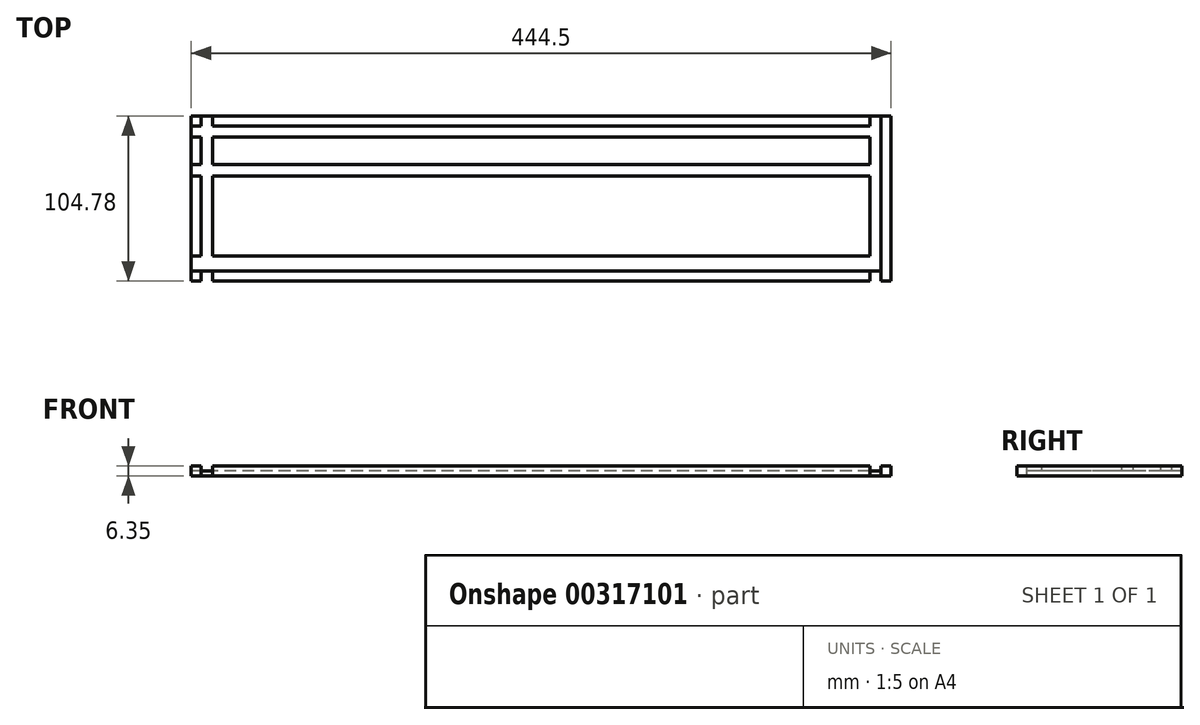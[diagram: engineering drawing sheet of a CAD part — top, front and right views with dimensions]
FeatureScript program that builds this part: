
annotation { "Feature Type Name" : "Feature", "Feature Type Description" : "" }
export const myFeature = defineFeature(function(context is Context, id is Id, definition is map)
    precondition{}
    {
        {
            var Q0;
            Q0=qCreatedBy(makeId("Top.planeOp"),FACE);
            var sketch = newSketch(context, id + "F0", { "sketchPlane" : qUnion([Q0])});
            skLineSegment(sketch, "E0.bottom", {"start": v(222.25, 52.39) * mm, "end": v(-222.25, 52.39) * mm});
            skLineSegment(sketch, "E0.top", {"start": v(222.25, -52.39) * mm, "end": v(-222.25, -52.39) * mm});
            skLineSegment(sketch, "E0.left", {"start": v(222.25, 52.39) * mm, "end": v(222.25, -52.39) * mm});
            skLineSegment(sketch, "E0.right", {"start": v(-222.25, 52.39) * mm, "end": v(-222.25, -52.39) * mm});
            skPoint(sketch, "E0.middle", {"position": v(0, 0) * mm});
            skLineSegment(sketch, "E1.0", {"start": v(-215.9, 52.39) * mm, "end": v(-215.9, -52.39) * mm});
            skLineSegment(sketch, "E2.0", {"start": v(-208.76, 52.39) * mm, "end": v(-208.76, -52.39) * mm});
            skLineSegment(sketch, "E3.0", {"start": v(215.9, 52.39) * mm, "end": v(215.9, -52.39) * mm});
            skLineSegment(sketch, "E4.0", {"start": v(208.76, 52.39) * mm, "end": v(208.76, -52.39) * mm});
            skLineSegment(sketch, "E5", {"start": v(215.9, -46.04) * mm, "end": v(-222.25, -46.04) * mm});
            skLineSegment(sketch, "E6.0", {"start": v(215.9, -36.51) * mm, "end": v(-222.25, -36.51) * mm});
            skLineSegment(sketch, "E7.0", {"start": v(215.9, 14.29) * mm, "end": v(-222.25, 14.29) * mm});
            skLineSegment(sketch, "E8.0", {"start": v(215.9, 21.43) * mm, "end": v(-222.25, 21.43) * mm});
            skLineSegment(sketch, "E9", {"start": v(215.9, 46.04) * mm, "end": v(-222.25, 46.04) * mm});
            skLineSegment(sketch, "E10.0", {"start": v(215.9, 38.9) * mm, "end": v(-222.25, 38.9) * mm});
            skSolve(sketch);
        }
        {
            var Q0;
            {var subQ0=sQuery(id+"F0.wireOp",EDGE,"E2.0");var subQ1=sQuery(id+"F0.wireOp",EDGE,"E0.bottom");var subQ2=makeQuery(id+"F0.imprint","INTERSECT",VERTEX,{"derivedFrom":[subQ1,subQ0]});Q0=makeQuery(id+"F0.imprint","IMPRINT",FACE,{"disambiguationData":[TD([[makeQuery(id+"F0.imprint","IMPRINT",EDGE,{"disambiguationData":[TD([[subQ2,1.0]])],"derivedFrom":subQ1}),1.0]])]});}
            var Q1;
            {var subQ0=sQuery(id+"F0.wireOp",EDGE,"E2.0");var subQ1=sQuery(id+"F0.wireOp",EDGE,"E0.top");var subQ2=makeQuery(id+"F0.imprint","INTERSECT",VERTEX,{"derivedFrom":[subQ1,subQ0]});Q1=makeQuery(id+"F0.imprint","IMPRINT",FACE,{"disambiguationData":[TD([[makeQuery(id+"F0.imprint","IMPRINT",EDGE,{"disambiguationData":[TD([[subQ2,1.0]])],"derivedFrom":subQ1}),-1.0]])]});}
            var Q2;
            {var subQ0=sQuery(id+"F0.wireOp",EDGE,"E7.0");var subQ1=sQuery(id+"F0.wireOp",EDGE,"E1.0");var subQ2=makeQuery(id+"F0.imprint","INTERSECT",VERTEX,{"derivedFrom":[subQ1,subQ0]});Q2=makeQuery(id+"F0.imprint","IMPRINT",FACE,{"disambiguationData":[TD([[makeQuery(id+"F0.imprint","IMPRINT",EDGE,{"disambiguationData":[TD([[subQ2,-1.0]])],"derivedFrom":subQ1}),1.0]])]});}
            var Q3;
            {var subQ0=sQuery(id+"F0.wireOp",EDGE,"E10.0");var subQ1=sQuery(id+"F0.wireOp",EDGE,"E1.0");var subQ2=makeQuery(id+"F0.imprint","INTERSECT",VERTEX,{"derivedFrom":[subQ1,subQ0]});Q3=makeQuery(id+"F0.imprint","IMPRINT",FACE,{"disambiguationData":[TD([[makeQuery(id+"F0.imprint","IMPRINT",EDGE,{"disambiguationData":[TD([[subQ2,-1.0]])],"derivedFrom":subQ1}),1.0]])]});}
            var Q4;
            {var subQ0=sQuery(id+"F0.wireOp",EDGE,"E9");var subQ1=sQuery(id+"F0.wireOp",EDGE,"E2.0");var subQ2=makeQuery(id+"F0.imprint","INTERSECT",VERTEX,{"derivedFrom":[subQ1,subQ0]});Q4=makeQuery(id+"F0.imprint","IMPRINT",FACE,{"disambiguationData":[TD([[makeQuery(id+"F0.imprint","IMPRINT",EDGE,{"disambiguationData":[TD([[subQ2,-1.0]])],"derivedFrom":subQ1}),1.0]])]});}
            var Q5;
            {var subQ0=sQuery(id+"F0.wireOp",EDGE,"E8.0");var subQ1=sQuery(id+"F0.wireOp",EDGE,"E2.0");var subQ2=makeQuery(id+"F0.imprint","INTERSECT",VERTEX,{"derivedFrom":[subQ1,subQ0]});Q5=makeQuery(id+"F0.imprint","IMPRINT",FACE,{"disambiguationData":[TD([[makeQuery(id+"F0.imprint","IMPRINT",EDGE,{"disambiguationData":[TD([[subQ2,-1.0]])],"derivedFrom":subQ1}),1.0]])]});}
            var Q6;
            {var subQ4=sQuery(id+"F0.wireOp",EDGE,"E0.left");Q6=makeQuery(id+"F0.imprint","IMPRINT",FACE,{"disambiguationData":[TD([[makeQuery(id+"F0.imprint","IMPRINT",EDGE,{"derivedFrom":subQ4}),-1.0]])]});}
            var Q7;
            {var subQ0=sQuery(id+"F0.wireOp",EDGE,"E6.0");var subQ1=sQuery(id+"F0.wireOp",EDGE,"E0.right");var subQ2=makeQuery(id+"F0.imprint","INTERSECT",VERTEX,{"derivedFrom":[subQ1,subQ0]});Q7=makeQuery(id+"F0.imprint","IMPRINT",FACE,{"disambiguationData":[TD([[makeQuery(id+"F0.imprint","IMPRINT",EDGE,{"disambiguationData":[TD([[subQ2,1.0]])],"derivedFrom":subQ1}),1.0]])]});}
            var Q8;
            {var subQ0=sQuery(id+"F0.wireOp",EDGE,"E6.0");var subQ1=sQuery(id+"F0.wireOp",EDGE,"E2.0");var subQ2=makeQuery(id+"F0.imprint","INTERSECT",VERTEX,{"derivedFrom":[subQ1,subQ0]});Q8=makeQuery(id+"F0.imprint","IMPRINT",FACE,{"disambiguationData":[TD([[makeQuery(id+"F0.imprint","IMPRINT",EDGE,{"disambiguationData":[TD([[subQ2,-1.0]])],"derivedFrom":subQ1}),1.0]])]});}
            var Q9;
            {var subQ0=sQuery(id+"F0.wireOp",EDGE,"E7.0");var subQ1=sQuery(id+"F0.wireOp",EDGE,"E2.0");var subQ2=makeQuery(id+"F0.imprint","INTERSECT",VERTEX,{"derivedFrom":[subQ1,subQ0]});Q9=makeQuery(id+"F0.imprint","IMPRINT",FACE,{"disambiguationData":[TD([[makeQuery(id+"F0.imprint","IMPRINT",EDGE,{"disambiguationData":[TD([[subQ2,-1.0]])],"derivedFrom":subQ1}),1.0]])]});}
            var Q10;
            {var subQ0=sQuery(id+"F0.wireOp",EDGE,"E10.0");var subQ1=sQuery(id+"F0.wireOp",EDGE,"E2.0");var subQ2=makeQuery(id+"F0.imprint","INTERSECT",VERTEX,{"derivedFrom":[subQ1,subQ0]});Q10=makeQuery(id+"F0.imprint","IMPRINT",FACE,{"disambiguationData":[TD([[makeQuery(id+"F0.imprint","IMPRINT",EDGE,{"disambiguationData":[TD([[subQ2,-1.0]])],"derivedFrom":subQ1}),1.0]])]});}
            var Q11;
            {var subQ0=sQuery(id+"F0.wireOp",EDGE,"E9");var subQ1=sQuery(id+"F0.wireOp",EDGE,"E0.right");var subQ2=makeQuery(id+"F0.imprint","INTERSECT",VERTEX,{"derivedFrom":[subQ1,subQ0]});Q11=makeQuery(id+"F0.imprint","IMPRINT",FACE,{"disambiguationData":[TD([[makeQuery(id+"F0.imprint","IMPRINT",EDGE,{"disambiguationData":[TD([[subQ2,-1.0]])],"derivedFrom":subQ1}),1.0]])]});}
            var Q12;
            {var subQ0=sQuery(id+"F0.wireOp",EDGE,"E1.0");var subQ1=sQuery(id+"F0.wireOp",EDGE,"E0.bottom");var subQ2=makeQuery(id+"F0.imprint","INTERSECT",VERTEX,{"derivedFrom":[subQ1,subQ0]});Q12=makeQuery(id+"F0.imprint","IMPRINT",FACE,{"disambiguationData":[TD([[makeQuery(id+"F0.imprint","IMPRINT",EDGE,{"disambiguationData":[TD([[subQ2,1.0]])],"derivedFrom":subQ1}),1.0]])]});}
            var Q13;
            {var subQ0=sQuery(id+"F0.wireOp",EDGE,"E3.0");var subQ1=sQuery(id+"F0.wireOp",EDGE,"E0.bottom");var subQ2=makeQuery(id+"F0.imprint","INTERSECT",VERTEX,{"derivedFrom":[subQ1,subQ0]});Q13=makeQuery(id+"F0.imprint","IMPRINT",FACE,{"disambiguationData":[TD([[makeQuery(id+"F0.imprint","IMPRINT",EDGE,{"disambiguationData":[TD([[subQ2,-1.0]])],"derivedFrom":subQ1}),1.0]])]});}
            var Q14;
            {var subQ0=sQuery(id+"F0.wireOp",EDGE,"E0.right");var subQ1=sQuery(id+"F0.wireOp",EDGE,"E0.bottom");var subQ2=makeQuery(id+"F0.imprint","INTERSECT",VERTEX,{"derivedFrom":[subQ1,subQ0]});Q14=makeQuery(id+"F0.imprint","IMPRINT",FACE,{"disambiguationData":[TD([[makeQuery(id+"F0.imprint","IMPRINT",EDGE,{"disambiguationData":[TD([[subQ2,1.0]])],"derivedFrom":subQ1}),1.0]])]});}
            var Q15;
            {var subQ0=sQuery(id+"F0.wireOp",EDGE,"E8.0");var subQ1=sQuery(id+"F0.wireOp",EDGE,"E1.0");var subQ2=makeQuery(id+"F0.imprint","INTERSECT",VERTEX,{"derivedFrom":[subQ1,subQ0]});Q15=makeQuery(id+"F0.imprint","IMPRINT",FACE,{"disambiguationData":[TD([[makeQuery(id+"F0.imprint","IMPRINT",EDGE,{"disambiguationData":[TD([[subQ2,-1.0]])],"derivedFrom":subQ1}),1.0]])]});}
            var Q16;
            {var subQ0=sQuery(id+"F0.wireOp",EDGE,"E9");var subQ1=sQuery(id+"F0.wireOp",EDGE,"E1.0");var subQ2=makeQuery(id+"F0.imprint","INTERSECT",VERTEX,{"derivedFrom":[subQ1,subQ0]});Q16=makeQuery(id+"F0.imprint","IMPRINT",FACE,{"disambiguationData":[TD([[makeQuery(id+"F0.imprint","IMPRINT",EDGE,{"disambiguationData":[TD([[subQ2,-1.0]])],"derivedFrom":subQ1}),1.0]])]});}
            var Q17;
            {var subQ0=sQuery(id+"F0.wireOp",EDGE,"E8.0");var subQ1=sQuery(id+"F0.wireOp",EDGE,"E3.0");var subQ2=makeQuery(id+"F0.imprint","INTERSECT",VERTEX,{"derivedFrom":[subQ1,subQ0]});Q17=makeQuery(id+"F0.imprint","IMPRINT",FACE,{"disambiguationData":[TD([[makeQuery(id+"F0.imprint","IMPRINT",EDGE,{"disambiguationData":[TD([[subQ2,1.0]])],"derivedFrom":subQ1}),-1.0]])]});}
            var Q18;
            {var subQ0=sQuery(id+"F0.wireOp",EDGE,"E8.0");var subQ1=sQuery(id+"F0.wireOp",EDGE,"E0.right");var subQ2=makeQuery(id+"F0.imprint","INTERSECT",VERTEX,{"derivedFrom":[subQ1,subQ0]});Q18=makeQuery(id+"F0.imprint","IMPRINT",FACE,{"disambiguationData":[TD([[makeQuery(id+"F0.imprint","IMPRINT",EDGE,{"disambiguationData":[TD([[subQ2,1.0]])],"derivedFrom":subQ1}),1.0]])]});}
            var Q19;
            {var subQ0=sQuery(id+"F0.wireOp",EDGE,"E7.0");var subQ1=sQuery(id+"F0.wireOp",EDGE,"E0.right");var subQ2=makeQuery(id+"F0.imprint","INTERSECT",VERTEX,{"derivedFrom":[subQ1,subQ0]});Q19=makeQuery(id+"F0.imprint","IMPRINT",FACE,{"disambiguationData":[TD([[makeQuery(id+"F0.imprint","IMPRINT",EDGE,{"disambiguationData":[TD([[subQ2,1.0]])],"derivedFrom":subQ1}),1.0]])]});}
            var Q20;
            {var subQ0=sQuery(id+"F0.wireOp",EDGE,"E5");var subQ1=sQuery(id+"F0.wireOp",EDGE,"E0.right");var subQ2=makeQuery(id+"F0.imprint","INTERSECT",VERTEX,{"derivedFrom":[subQ1,subQ0]});Q20=makeQuery(id+"F0.imprint","IMPRINT",FACE,{"disambiguationData":[TD([[makeQuery(id+"F0.imprint","IMPRINT",EDGE,{"disambiguationData":[TD([[subQ2,1.0]])],"derivedFrom":subQ1}),1.0]])]});}
            var Q21;
            {var subQ0=sQuery(id+"F0.wireOp",EDGE,"E5");var subQ1=sQuery(id+"F0.wireOp",EDGE,"E3.0");var subQ2=makeQuery(id+"F0.imprint","INTERSECT",VERTEX,{"derivedFrom":[subQ1,subQ0]});Q21=makeQuery(id+"F0.imprint","IMPRINT",FACE,{"disambiguationData":[TD([[makeQuery(id+"F0.imprint","IMPRINT",EDGE,{"disambiguationData":[TD([[subQ2,1.0]])],"derivedFrom":subQ1}),-1.0]])]});}
            var Q22;
            {var subQ0=sQuery(id+"F0.wireOp",EDGE,"E9");var subQ1=sQuery(id+"F0.wireOp",EDGE,"E3.0");var subQ2=makeQuery(id+"F0.imprint","INTERSECT",VERTEX,{"derivedFrom":[subQ1,subQ0]});Q22=makeQuery(id+"F0.imprint","IMPRINT",FACE,{"disambiguationData":[TD([[makeQuery(id+"F0.imprint","IMPRINT",EDGE,{"disambiguationData":[TD([[subQ2,-1.0]])],"derivedFrom":subQ1}),-1.0]])]});}
            var Q23;
            {var subQ0=sQuery(id+"F0.wireOp",EDGE,"E7.0");var subQ1=sQuery(id+"F0.wireOp",EDGE,"E3.0");var subQ2=makeQuery(id+"F0.imprint","INTERSECT",VERTEX,{"derivedFrom":[subQ1,subQ0]});Q23=makeQuery(id+"F0.imprint","IMPRINT",FACE,{"disambiguationData":[TD([[makeQuery(id+"F0.imprint","IMPRINT",EDGE,{"disambiguationData":[TD([[subQ2,1.0]])],"derivedFrom":subQ1}),-1.0]])]});}
            var Q24;
            {var subQ0=sQuery(id+"F0.wireOp",EDGE,"E6.0");var subQ1=sQuery(id+"F0.wireOp",EDGE,"E1.0");var subQ2=makeQuery(id+"F0.imprint","INTERSECT",VERTEX,{"derivedFrom":[subQ1,subQ0]});Q24=makeQuery(id+"F0.imprint","IMPRINT",FACE,{"disambiguationData":[TD([[makeQuery(id+"F0.imprint","IMPRINT",EDGE,{"disambiguationData":[TD([[subQ2,-1.0]])],"derivedFrom":subQ1}),1.0]])]});}
            var Q25;
            {var subQ0=sQuery(id+"F0.wireOp",EDGE,"E0.right");var subQ1=sQuery(id+"F0.wireOp",EDGE,"E0.top");var subQ2=makeQuery(id+"F0.imprint","INTERSECT",VERTEX,{"derivedFrom":[subQ1,subQ0]});Q25=makeQuery(id+"F0.imprint","IMPRINT",FACE,{"disambiguationData":[TD([[makeQuery(id+"F0.imprint","IMPRINT",EDGE,{"disambiguationData":[TD([[subQ2,1.0]])],"derivedFrom":subQ1}),-1.0]])]});}
            var Q26;
            {var subQ0=sQuery(id+"F0.wireOp",EDGE,"E6.0");var subQ1=sQuery(id+"F0.wireOp",EDGE,"E3.0");var subQ2=makeQuery(id+"F0.imprint","INTERSECT",VERTEX,{"derivedFrom":[subQ1,subQ0]});Q26=makeQuery(id+"F0.imprint","IMPRINT",FACE,{"disambiguationData":[TD([[makeQuery(id+"F0.imprint","IMPRINT",EDGE,{"disambiguationData":[TD([[subQ2,1.0]])],"derivedFrom":subQ1}),-1.0]])]});}
            var Q27;
            Q27=sQuery(id+"F0.wireOp",EDGE,"E0.right");
            var Q28;
            Q28=sQuery(id+"F0.wireOp",EDGE,"E0.bottom");
            var Q29;
            Q29=sQuery(id+"F0.wireOp",EDGE,"E0.top");
            var Q30;
            Q30=sQuery(id+"F0.wireOp",EDGE,"E0.left");
            extrude(context, id + "F1", {"entities" : qUnion([Q0, Q1, Q2, Q3, Q4, Q5, Q6, Q7, Q8, Q9, Q10, Q11, Q12, Q13, Q14, Q15, Q16, Q17, Q18, Q19, Q20, Q21, Q22, Q23, Q24, Q25, Q26]), "surfaceEntities" : qUnion([Q27, Q28, Q29, Q30]), "oppositeDirection" : true, "depth" : 6.35 * mm});
        }
        {
            var Q0;
            {var subQ0=sQuery(id+"F0.wireOp",EDGE,"E6.0");var subQ1=sQuery(id+"F0.wireOp",EDGE,"E1.0");var subQ2=makeQuery(id+"F0.imprint","INTERSECT",VERTEX,{"derivedFrom":[subQ1,subQ0]});Q0=makeQuery(id+"F0.imprint","IMPRINT",FACE,{"disambiguationData":[TD([[makeQuery(id+"F0.imprint","IMPRINT",EDGE,{"disambiguationData":[TD([[subQ2,-1.0]])],"derivedFrom":subQ1}),1.0]])]});}
            var Q1;
            {var subQ0=sQuery(id+"F0.wireOp",EDGE,"E7.0");var subQ1=sQuery(id+"F0.wireOp",EDGE,"E1.0");var subQ2=makeQuery(id+"F0.imprint","INTERSECT",VERTEX,{"derivedFrom":[subQ1,subQ0]});Q1=makeQuery(id+"F0.imprint","IMPRINT",FACE,{"disambiguationData":[TD([[makeQuery(id+"F0.imprint","IMPRINT",EDGE,{"disambiguationData":[TD([[subQ2,-1.0]])],"derivedFrom":subQ1}),1.0]])]});}
            var Q2;
            {var subQ0=sQuery(id+"F0.wireOp",EDGE,"E8.0");var subQ1=sQuery(id+"F0.wireOp",EDGE,"E1.0");var subQ2=makeQuery(id+"F0.imprint","INTERSECT",VERTEX,{"derivedFrom":[subQ1,subQ0]});Q2=makeQuery(id+"F0.imprint","IMPRINT",FACE,{"disambiguationData":[TD([[makeQuery(id+"F0.imprint","IMPRINT",EDGE,{"disambiguationData":[TD([[subQ2,-1.0]])],"derivedFrom":subQ1}),1.0]])]});}
            var Q3;
            {var subQ0=sQuery(id+"F0.wireOp",EDGE,"E10.0");var subQ1=sQuery(id+"F0.wireOp",EDGE,"E1.0");var subQ2=makeQuery(id+"F0.imprint","INTERSECT",VERTEX,{"derivedFrom":[subQ1,subQ0]});Q3=makeQuery(id+"F0.imprint","IMPRINT",FACE,{"disambiguationData":[TD([[makeQuery(id+"F0.imprint","IMPRINT",EDGE,{"disambiguationData":[TD([[subQ2,-1.0]])],"derivedFrom":subQ1}),1.0]])]});}
            var Q4;
            {var subQ0=sQuery(id+"F0.wireOp",EDGE,"E9");var subQ1=sQuery(id+"F0.wireOp",EDGE,"E1.0");var subQ2=makeQuery(id+"F0.imprint","INTERSECT",VERTEX,{"derivedFrom":[subQ1,subQ0]});Q4=makeQuery(id+"F0.imprint","IMPRINT",FACE,{"disambiguationData":[TD([[makeQuery(id+"F0.imprint","IMPRINT",EDGE,{"disambiguationData":[TD([[subQ2,-1.0]])],"derivedFrom":subQ1}),1.0]])]});}
            var Q5;
            {var subQ0=sQuery(id+"F0.wireOp",EDGE,"E1.0");var subQ1=sQuery(id+"F0.wireOp",EDGE,"E0.bottom");var subQ2=makeQuery(id+"F0.imprint","INTERSECT",VERTEX,{"derivedFrom":[subQ1,subQ0]});Q5=makeQuery(id+"F0.imprint","IMPRINT",FACE,{"disambiguationData":[TD([[makeQuery(id+"F0.imprint","IMPRINT",EDGE,{"disambiguationData":[TD([[subQ2,1.0]])],"derivedFrom":subQ1}),1.0]])]});}
            var Q6;
            {var subQ0=sQuery(id+"F0.wireOp",EDGE,"E9");var subQ1=sQuery(id+"F0.wireOp",EDGE,"E0.right");var subQ2=makeQuery(id+"F0.imprint","INTERSECT",VERTEX,{"derivedFrom":[subQ1,subQ0]});Q6=makeQuery(id+"F0.imprint","IMPRINT",FACE,{"disambiguationData":[TD([[makeQuery(id+"F0.imprint","IMPRINT",EDGE,{"disambiguationData":[TD([[subQ2,-1.0]])],"derivedFrom":subQ1}),1.0]])]});}
            var Q7;
            {var subQ0=sQuery(id+"F0.wireOp",EDGE,"E7.0");var subQ1=sQuery(id+"F0.wireOp",EDGE,"E0.right");var subQ2=makeQuery(id+"F0.imprint","INTERSECT",VERTEX,{"derivedFrom":[subQ1,subQ0]});Q7=makeQuery(id+"F0.imprint","IMPRINT",FACE,{"disambiguationData":[TD([[makeQuery(id+"F0.imprint","IMPRINT",EDGE,{"disambiguationData":[TD([[subQ2,1.0]])],"derivedFrom":subQ1}),1.0]])]});}
            var Q8;
            {var subQ0=sQuery(id+"F0.wireOp",EDGE,"E8.0");var subQ1=sQuery(id+"F0.wireOp",EDGE,"E2.0");var subQ2=makeQuery(id+"F0.imprint","INTERSECT",VERTEX,{"derivedFrom":[subQ1,subQ0]});Q8=makeQuery(id+"F0.imprint","IMPRINT",FACE,{"disambiguationData":[TD([[makeQuery(id+"F0.imprint","IMPRINT",EDGE,{"disambiguationData":[TD([[subQ2,-1.0]])],"derivedFrom":subQ1}),1.0]])]});}
            var Q9;
            {var subQ0=sQuery(id+"F0.wireOp",EDGE,"E9");var subQ1=sQuery(id+"F0.wireOp",EDGE,"E2.0");var subQ2=makeQuery(id+"F0.imprint","INTERSECT",VERTEX,{"derivedFrom":[subQ1,subQ0]});Q9=makeQuery(id+"F0.imprint","IMPRINT",FACE,{"disambiguationData":[TD([[makeQuery(id+"F0.imprint","IMPRINT",EDGE,{"disambiguationData":[TD([[subQ2,-1.0]])],"derivedFrom":subQ1}),1.0]])]});}
            var Q10;
            {var subQ0=sQuery(id+"F0.wireOp",EDGE,"E5");var subQ1=sQuery(id+"F0.wireOp",EDGE,"E0.right");var subQ2=makeQuery(id+"F0.imprint","INTERSECT",VERTEX,{"derivedFrom":[subQ1,subQ0]});Q10=makeQuery(id+"F0.imprint","IMPRINT",FACE,{"disambiguationData":[TD([[makeQuery(id+"F0.imprint","IMPRINT",EDGE,{"disambiguationData":[TD([[subQ2,1.0]])],"derivedFrom":subQ1}),1.0]])]});}
            var Q11;
            {var subQ0=sQuery(id+"F0.wireOp",EDGE,"E6.0");var subQ1=sQuery(id+"F0.wireOp",EDGE,"E2.0");var subQ2=makeQuery(id+"F0.imprint","INTERSECT",VERTEX,{"derivedFrom":[subQ1,subQ0]});Q11=makeQuery(id+"F0.imprint","IMPRINT",FACE,{"disambiguationData":[TD([[makeQuery(id+"F0.imprint","IMPRINT",EDGE,{"disambiguationData":[TD([[subQ2,-1.0]])],"derivedFrom":subQ1}),1.0]])]});}
            var Q12;
            {var subQ0=sQuery(id+"F0.wireOp",EDGE,"E5");var subQ1=sQuery(id+"F0.wireOp",EDGE,"E3.0");var subQ2=makeQuery(id+"F0.imprint","INTERSECT",VERTEX,{"derivedFrom":[subQ1,subQ0]});Q12=makeQuery(id+"F0.imprint","IMPRINT",FACE,{"disambiguationData":[TD([[makeQuery(id+"F0.imprint","IMPRINT",EDGE,{"disambiguationData":[TD([[subQ2,1.0]])],"derivedFrom":subQ1}),-1.0]])]});}
            var Q13;
            {var subQ0=sQuery(id+"F0.wireOp",EDGE,"E7.0");var subQ1=sQuery(id+"F0.wireOp",EDGE,"E3.0");var subQ2=makeQuery(id+"F0.imprint","INTERSECT",VERTEX,{"derivedFrom":[subQ1,subQ0]});Q13=makeQuery(id+"F0.imprint","IMPRINT",FACE,{"disambiguationData":[TD([[makeQuery(id+"F0.imprint","IMPRINT",EDGE,{"disambiguationData":[TD([[subQ2,1.0]])],"derivedFrom":subQ1}),-1.0]])]});}
            var Q14;
            {var subQ0=sQuery(id+"F0.wireOp",EDGE,"E9");var subQ1=sQuery(id+"F0.wireOp",EDGE,"E3.0");var subQ2=makeQuery(id+"F0.imprint","INTERSECT",VERTEX,{"derivedFrom":[subQ1,subQ0]});Q14=makeQuery(id+"F0.imprint","IMPRINT",FACE,{"disambiguationData":[TD([[makeQuery(id+"F0.imprint","IMPRINT",EDGE,{"disambiguationData":[TD([[subQ2,-1.0]])],"derivedFrom":subQ1}),-1.0]])]});}
            var Q15;
            {var subQ0=sQuery(id+"F0.wireOp",EDGE,"E3.0");var subQ1=sQuery(id+"F0.wireOp",EDGE,"E0.bottom");var subQ2=makeQuery(id+"F0.imprint","INTERSECT",VERTEX,{"derivedFrom":[subQ1,subQ0]});Q15=makeQuery(id+"F0.imprint","IMPRINT",FACE,{"disambiguationData":[TD([[makeQuery(id+"F0.imprint","IMPRINT",EDGE,{"disambiguationData":[TD([[subQ2,-1.0]])],"derivedFrom":subQ1}),1.0]])]});}
            var Q16;
            {var subQ0=sQuery(id+"F0.wireOp",EDGE,"E8.0");var subQ1=sQuery(id+"F0.wireOp",EDGE,"E3.0");var subQ2=makeQuery(id+"F0.imprint","INTERSECT",VERTEX,{"derivedFrom":[subQ1,subQ0]});Q16=makeQuery(id+"F0.imprint","IMPRINT",FACE,{"disambiguationData":[TD([[makeQuery(id+"F0.imprint","IMPRINT",EDGE,{"disambiguationData":[TD([[subQ2,1.0]])],"derivedFrom":subQ1}),-1.0]])]});}
            var Q17;
            {var subQ0=sQuery(id+"F0.wireOp",EDGE,"E6.0");var subQ1=sQuery(id+"F0.wireOp",EDGE,"E3.0");var subQ2=makeQuery(id+"F0.imprint","INTERSECT",VERTEX,{"derivedFrom":[subQ1,subQ0]});Q17=makeQuery(id+"F0.imprint","IMPRINT",FACE,{"disambiguationData":[TD([[makeQuery(id+"F0.imprint","IMPRINT",EDGE,{"disambiguationData":[TD([[subQ2,1.0]])],"derivedFrom":subQ1}),-1.0]])]});}
            extrude(context, id + "F2", {"entities" : qUnion([Q0, Q1, Q2, Q3, Q4, Q5, Q6, Q7, Q8, Q9, Q10, Q11, Q12, Q13, Q14, Q15, Q16, Q17]), "operationType" : NewBodyOperationType.REMOVE, "oppositeDirection" : true, "depth" : 3.17 * mm});
        }
    });
